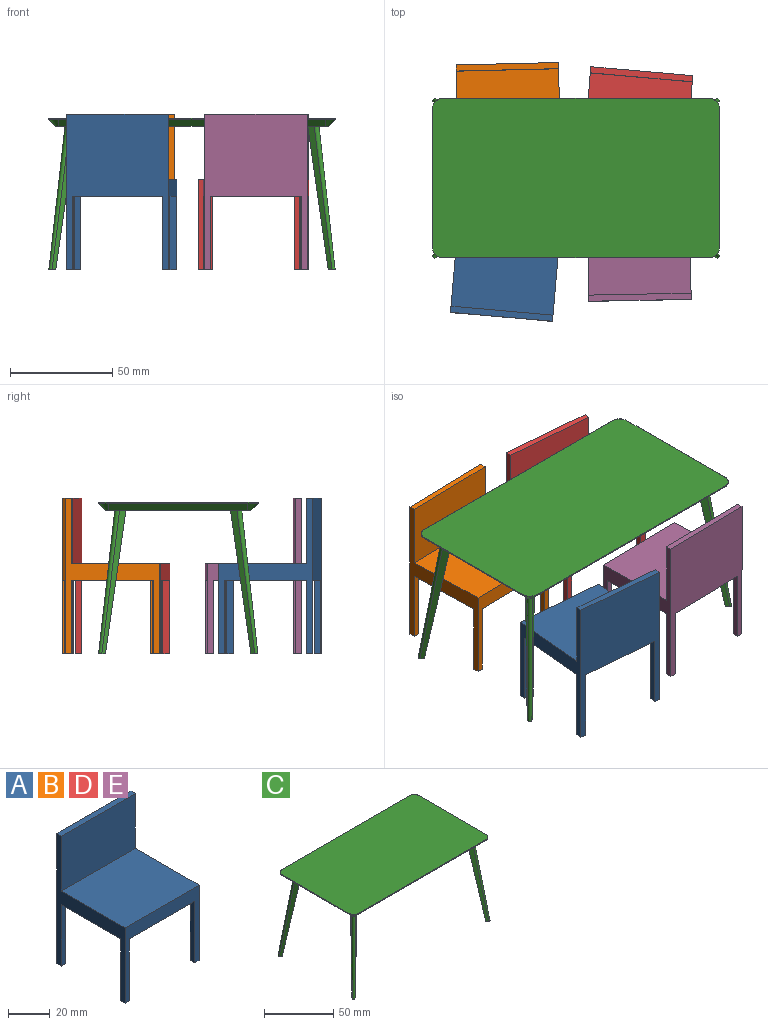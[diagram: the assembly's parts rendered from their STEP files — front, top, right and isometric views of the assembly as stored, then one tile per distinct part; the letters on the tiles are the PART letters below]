
ASSEMBLY  parts=5 mates=4
PART A: 20 faces, bbox 50x46x76 mm
  f0: plane 3x3mm, normal (0,0,-1), area 9mm2, adj f2,f6,f15,f19
  f1: plane 3x3mm, normal (0,0,-1), area 9mm2, adj f3,f4,f15,f16
  f2: plane 36x3mm, normal (0,-1,0), area 108mm2, adj f0,f9,f15,f19
  f3: plane 36x3mm, normal (0,1,0), area 108mm2, adj f1,f9,f15,f16
  f4: plane 50x44mm, normal (0,-1,0), area 616mm2, adj f1,f9,f11,f12,f14,f15,f16,f17
  f5: plane 50x3mm, normal (0,0,1), area 150mm2, adj f6,f13,f14,f15
  f6: plane 76x50mm, normal (0,1,0), area 2216mm2, adj f0,f5,f7,f9,f14,f15,f18,f19
  f7: plane 3x3mm, normal (0,0,-1), area 9mm2, adj f6,f8,f14,f18
  f8: plane 36x3mm, normal (0,-1,0), area 108mm2, adj f7,f9,f14,f18
  f9: plane 50x46mm, normal (0,0,-1), area 2264mm2, adj f2,f3,f4,f6,f8,f10,f14,f15
  f10: plane 36x3mm, normal (0,1,0), area 108mm2, adj f9,f11,f14,f17
  f11: plane 3x3mm, normal (0,0,-1), area 9mm2, adj f4,f10,f14,f17
  f12: plane 50x43mm, normal (0,0,1), area 2150mm2, adj f4,f13,f14,f15
  f13: plane 50x32mm, normal (0,-1,0), area 1600mm2, adj f5,f12,f14,f15
  f14: plane 76x46mm, normal (1,0,0), area 680mm2, adj f4,f5,f6,f7,f8,f9,f10,f11
  f15: plane 76x46mm, normal (-1,0,0), area 680mm2, adj f0,f1,f2,f3,f4,f5,f6,f9
  f16: plane 36x3mm, normal (1,0,0), area 108mm2, adj f1,f3,f4,f9
  f17: plane 36x3mm, normal (-1,0,0), area 108mm2, adj f4,f9,f10,f11
  f18: plane 36x3mm, normal (-1,0,0), area 108mm2, adj f6,f7,f8,f9
  f19: plane 36x3mm, normal (1,0,0), area 108mm2, adj f0,f2,f6,f9
PART B: same geometry as A
PART C: 38 faces, bbox 140x78x74 mm
  f0: plane 68x0.5mm, normal (-1,0,0), area 34mm2, adj f4,f6,f9,f13
  f1: plane 130x0.5mm, normal (0,-1,0), area 65mm2, adj f4,f6,f7,f10
  f2: plane 68x0.5mm, normal (1,0,0), area 34mm2, adj f4,f7,f8,f14
  f3: plane 130x0.5mm, normal (0,1,0), area 65mm2, adj f4,f8,f9,f17
  f4: plane 140x78mm, normal (0,0,1), area 10898.5mm2, adj f0,f1,f2,f3,f6,f7,f8,f9
  f5: plane 133.02x71.02mm, normal (0,0,-1), area 9375.7mm2, adj f10,f11,f12,f13,f14,f15,f16,f17
  f6: cylinder r=5mm len=5mm, axis (0,0,1), area 3.9mm2, adj f0,f1,f4,f11
  f7: cylinder r=5mm len=5mm, axis (0,0,-1), area 3.9mm2, adj f1,f2,f4,f12
  f8: cylinder r=5mm len=5mm, axis (0,0,1), area 3.9mm2, adj f2,f3,f4,f16
  f9: cylinder r=5mm len=5mm, axis (0,0,-1), area 3.9mm2, adj f0,f3,f4,f15
  f10: plane 130x3.5mm, normal (0,-0.71,-0.71), area 643.5mm2, adj f1,f5,f11,f12
  f11: cone r=1.5mm half-angle=45deg, axis (0,0,1), area 25.3mm2, adj f5,f6,f10,f13
  f12: cone r=1.5mm half-angle=45deg, axis (0,0,1), area 25.3mm2, adj f5,f7,f10,f14
  f13: plane 68x3.5mm, normal (-0.71,0,-0.71), area 336.6mm2, adj f0,f5,f11,f15
  f14: plane 68x3.5mm, normal (0.71,0,-0.71), area 336.6mm2, adj f2,f5,f12,f16
  f15: cone r=1.5mm half-angle=45deg, axis (0,0,1), area 25.3mm2, adj f5,f9,f13,f17
  f16: cone r=1.5mm half-angle=45deg, axis (0,0,1), area 25.3mm2, adj f5,f8,f14,f17
  f17: plane 130x3.5mm, normal (0,0.71,-0.71), area 643.5mm2, adj f3,f5,f15,f16
  f18: plane 3.4x3.4mm, normal (0,0,-1), area 6.3mm2, adj f19,f20,f21,f22
  f19: plane 70x11.79mm, normal (-0.57,-0.82,0.02), area 211mm2, adj f5,f18,f20,f22
  f20: bspline ~70x11.26mm, area 246mm2, adj f5,f18,f19,f21
  f21: plane 70x11.79mm, normal (0.82,0.57,0.02), area 211mm2, adj f5,f18,f20,f22
  f22: plane 70x11.92mm, normal (-0.69,0.69,-0.19), area 250mm2, adj f5,f18,f19,f21
  f23: plane 3.4x3.4mm, normal (0,0,-1), area 6.3mm2, adj f24,f25,f26,f27
  f24: plane 70x11.79mm, normal (-0.57,0.82,0.02), area 211mm2, adj f5,f23,f25,f27
  f25: bspline ~70x11.26mm, area 246mm2, adj f5,f23,f24,f26
  f26: plane 70x11.79mm, normal (0.82,-0.57,0.02), area 211mm2, adj f5,f23,f25,f27
  f27: plane 70x11.92mm, normal (-0.69,-0.69,-0.19), area 250mm2, adj f5,f23,f24,f26
  f28: plane 3.4x3.4mm, normal (0,0,-1), area 6.3mm2, adj f29,f30,f31,f32
  f29: plane 70x11.79mm, normal (0.57,-0.82,0.02), area 211mm2, adj f5,f28,f30,f32
  f30: bspline ~70x11.26mm, area 246mm2, adj f5,f28,f29,f31
  f31: plane 70x11.79mm, normal (-0.82,0.57,0.02), area 211mm2, adj f5,f28,f30,f32
  f32: plane 70x11.92mm, normal (0.69,0.69,-0.19), area 250mm2, adj f5,f28,f29,f31
  f33: plane 3.4x3.4mm, normal (0,0,-1), area 6.3mm2, adj f34,f35,f36,f37
  f34: plane 70x11.79mm, normal (0.57,0.82,0.02), area 211mm2, adj f5,f33,f35,f37
  f35: bspline ~70x11.26mm, area 246mm2, adj f5,f33,f34,f36
  f36: plane 70x11.79mm, normal (-0.82,-0.57,0.02), area 211mm2, adj f5,f33,f35,f37
  f37: plane 70x11.92mm, normal (0.69,-0.69,-0.19), area 250mm2, adj f5,f33,f34,f36
PART D: same geometry as A
PART E: same geometry as A
PLACE A rot(axis=(0,0,1),175deg) t=(-30.66,-1.96,0)mm
PLACE B rot(axis=(0,0,1),1.3deg) t=(-32.02,-10.12,0)mm
PLACE C at identity fixed
PLACE D rot(axis=(0,0,-1),5deg) t=(26.41,-13.54,0)mm
PLACE E rot(axis=(0,0,-1),178.9deg) t=(30.01,6.32,0)mm
MATE planar E.f11 <-> C.f18  axis (0,0,-1) through (5.39,-14.15,0)mm
MATE planar B.f11 <-> C.f18  axis (0,0,-1) through (-7.5,10.46,0)mm
MATE planar D.f1 <-> C.f18  axis (0,0,-1) through (3.25,8.56,0)mm
MATE planar A.f1 <-> C.f18  axis (0,0,-1) through (-7.5,-24.06,0)mm
